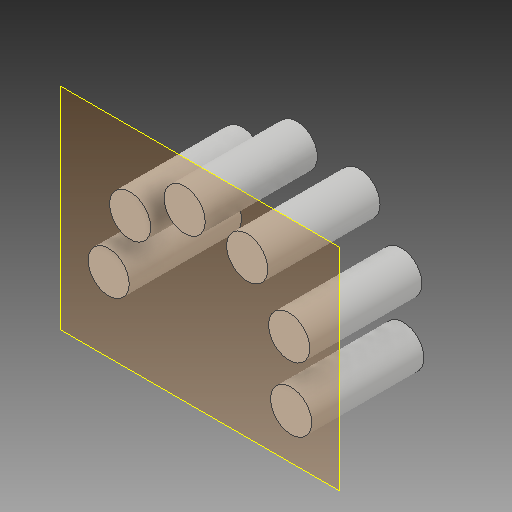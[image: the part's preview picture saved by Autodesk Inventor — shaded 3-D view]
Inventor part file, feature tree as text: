
AUTODESK INVENTOR PART (.ipt)
format: ipt  version: 2019.3 (Build 233278000, 278)  size: 122,368 bytes
history: native  units: mm
features: other x3, plane x1, extrude x1, sketch x1, reference x1
ambient origin geometry x8: Origin, YZ Plane, XZ Plane, XY Plane, X Axis, Y Axis, Z Axis, Center Point
bodies: Solid1 (feature_tree)
feature tree (7):
  plane  "Work Plane1"
  extrude  "Extrusion1"  [1 undecoded]
  sketch  "Sketch1"  dims[d0=30.0mm d1=0.0mm]
  reference  "Reference1"
  parser-record x1  (decoder bookkeeping rows leaked as tree rows — omitted from the tree; the rows remain in map.json)
  other  "mount assem.iam"
  other  "mounter:1"
note: 1 required parameter value undecoded (feature->parameter linkage not recoverable at this tier; creation-order binding heuristic only, values carry confidence <= 0.55)
note: 1 file-system path scrubbed to <path> (originals preserved in map.json)
